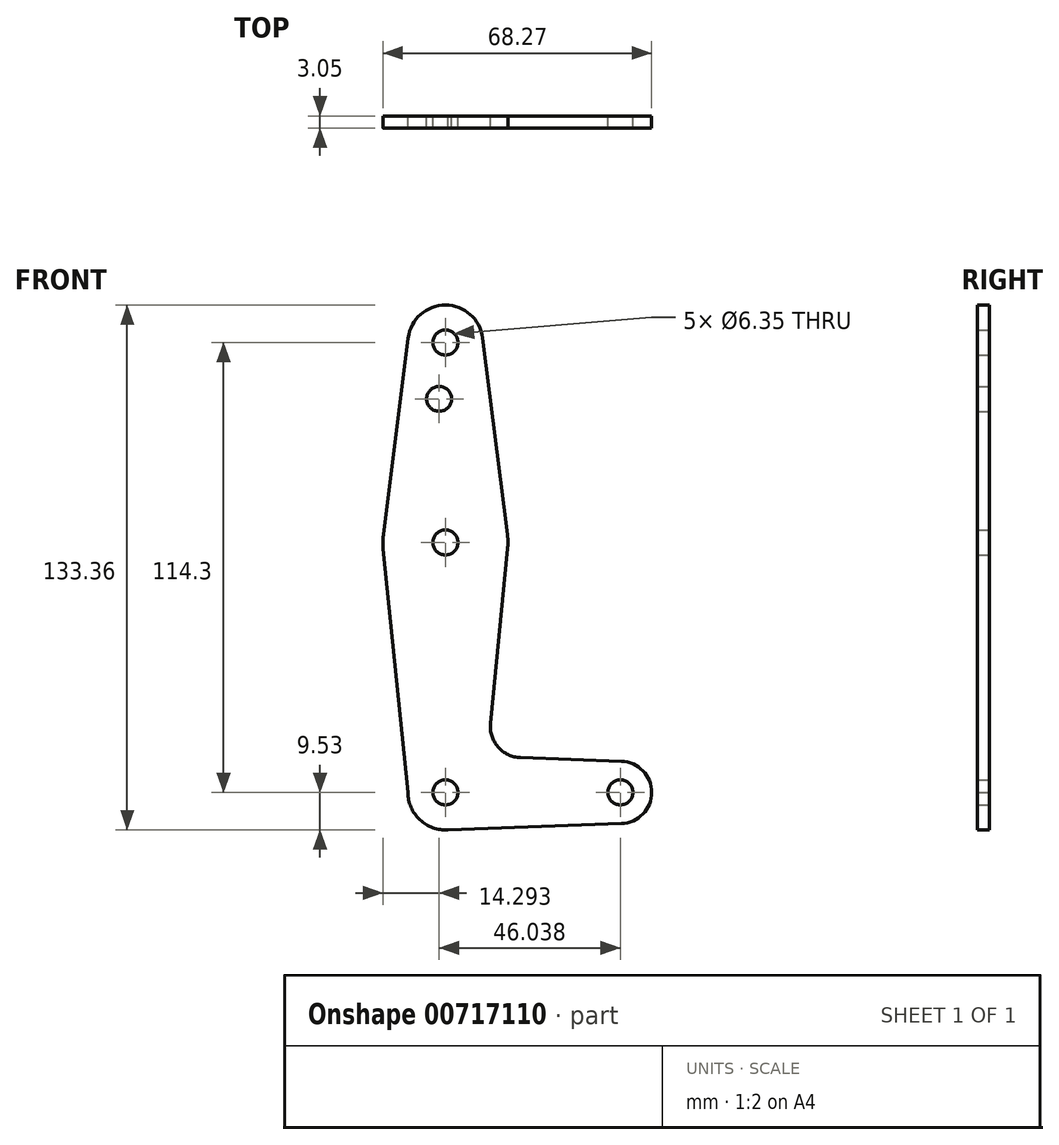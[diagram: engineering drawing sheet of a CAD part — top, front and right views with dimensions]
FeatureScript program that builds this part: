
annotation { "Feature Type Name" : "Feature", "Feature Type Description" : "" }
export const myFeature = defineFeature(function(context is Context, id is Id, definition is map)
    precondition{}
    {
        {
            var Q0;
            Q0=qCreatedBy(makeId("Front.planeOp"),FACE);
            var sketch = newSketch(context, id + "F0", { "sketchPlane" : qUnion([Q0])});
            skLineSegment(sketch, "E0", {"start": v(0, 114.3) * mm, "end": v(0, 0) * mm, "construction": true});
            skLineSegment(sketch, "E1", {"start": v(0, 0) * mm, "end": v(44.45, 0) * mm});
            skCircle(sketch, "E2", {"center": v(44.45, 0) * mm, "radius": 7.94 * mm});
            skCircle(sketch, "E3", {"center": v(0, 0) * mm, "radius": 9.53 * mm});
            skCircle(sketch, "E4", {"center": v(0, 63.5) * mm, "radius": 15.88 * mm});
            skCircle(sketch, "E5", {"center": v(0, 114.3) * mm, "radius": 9.53 * mm});
            skLineSegment(sketch, "E6", {"start": v(9.45, 115.5) * mm, "end": v(15.75, 65.48) * mm});
            skLineSegment(sketch, "E7", {"start": v(-9.45, 115.5) * mm, "end": v(-15.75, 65.48) * mm});
            skLineSegment(sketch, "E8", {"start": v(15.8, 61.95) * mm, "end": v(11.44, 17.57) * mm});
            skLineSegment(sketch, "E9", {"start": v(19.07, 8.85) * mm, "end": v(44.73, 7.93) * mm});
            skLineSegment(sketch, "E10", {"start": v(0, -9.52) * mm, "end": v(44.73, -7.93) * mm});
            skCircle(sketch, "E11", {"center": v(0, 114.3) * mm, "radius": 3.18 * mm});
            skCircle(sketch, "E12", {"center": v(-1.59, 100) * mm, "radius": 3.18 * mm});
            skCircle(sketch, "E13", {"center": v(0, 63.5) * mm, "radius": 3.18 * mm});
            skCircle(sketch, "E14", {"center": v(0, 0) * mm, "radius": 3.18 * mm});
            skCircle(sketch, "E15", {"center": v(44.45, 0) * mm, "radius": 3.18 * mm});
            skArc(sketch, "E16.filletArc", {"start": v(11.44, 17.57) * mm, "mid": v(13.37, 11.56) * mm, "end": v(19.07, 8.85) * mm});
            skLineSegment(sketch, "E17", {"start": v(-15.8, 61.9) * mm, "end": v(-9.52, 0) * mm});
            skSolve(sketch);
        }
        {
            var Q0;
            Q0 = qSketchRegion(id + "F0", true);
            var Q1;
            {var subQ0=sQuery(id+"F0.wireOp",EDGE,"E3");var subQ1=sQuery(id+"F0.wireOp",EDGE,"E0");var subQ2=makeQuery(id+"F0.imprint","INTERSECT",VERTEX,{"derivedFrom":[subQ1,subQ0]});Q1=makeQuery(id+"F0.imprint","IMPRINT",FACE,{"disambiguationData":[TD([[makeQuery(id+"F0.imprint","IMPRINT",EDGE,{"disambiguationData":[TD([[subQ2,-1.0]])],"derivedFrom":subQ1}),1.0]])]});}
            extrude(context, id + "F1", {"entities" : qUnion([Q0, Q1]), "depth" : 3.05 * mm, "offsetDistance" : 25.4 * mm});
        }
    });
